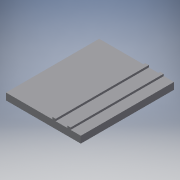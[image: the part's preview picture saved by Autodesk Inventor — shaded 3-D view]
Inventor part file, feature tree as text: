
AUTODESK INVENTOR PART (.ipt)
format: ipt  version: 2018.3 (Build 223284000, 284)  size: 110,592 bytes
history: native  units: mm
features: extrude x2, sketch x2
ambient origin geometry x8: Origin, YZ Plane, XZ Plane, XY Plane, X Axis, Y Axis, Z Axis, Center Point
bodies: Solid1 (feature_tree)
feature tree (4):
  extrude  "Extrusion1"  Depth=13.7mm
  extrude  "Extrusion2"  Depth=0.5mm
  sketch  "Sketch1"  dims[d0=11.0mm d1=13.7mm]
  sketch  "Sketch2"  dims[d2=1.0mm d3=0.0mm d4=0.5mm d5=0.5mm d6=1.7mm d7=0.3mm d8=0.0mm d9=1.5mm]
